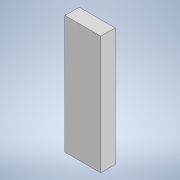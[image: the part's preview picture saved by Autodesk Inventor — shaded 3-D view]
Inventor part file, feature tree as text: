
AUTODESK INVENTOR PART (.ipt)
format: ipt  version: 2021.2 (Build 252289000, 289)  size: 107,520 bytes
history: native  units: in
note: dims shown in document units (in); Inventor stores cm internally (conversion verified against a paired STEP export)
features: extrude x3, sketch x3
ambient origin geometry x8: Origin, YZ Plane, XZ Plane, XY Plane, X Axis, Y Axis, Z Axis, Center Point
bodies: Solid1 (feature_tree)
feature tree (6):
  extrude  "Extrusion1"  Depth=3.0in
  extrude  "Extrusion3"  Depth=0.4in TaperAngle=0.0deg
  extrude  "Extrusion4"  [1 undecoded]
  sketch  "Sketch1"  dims[d0=1.0in d1=3.0in]
  sketch  "Sketch3"  dims[d2=0.4in d3=0.0in d6=0.13in d7=0.0in]
  sketch  "Sketch4"  dims[d8=0.18in d9=0.0in]
note: 1 required parameter value undecoded (feature->parameter linkage not recoverable at this tier; creation-order binding heuristic only, values carry confidence <= 0.55)
